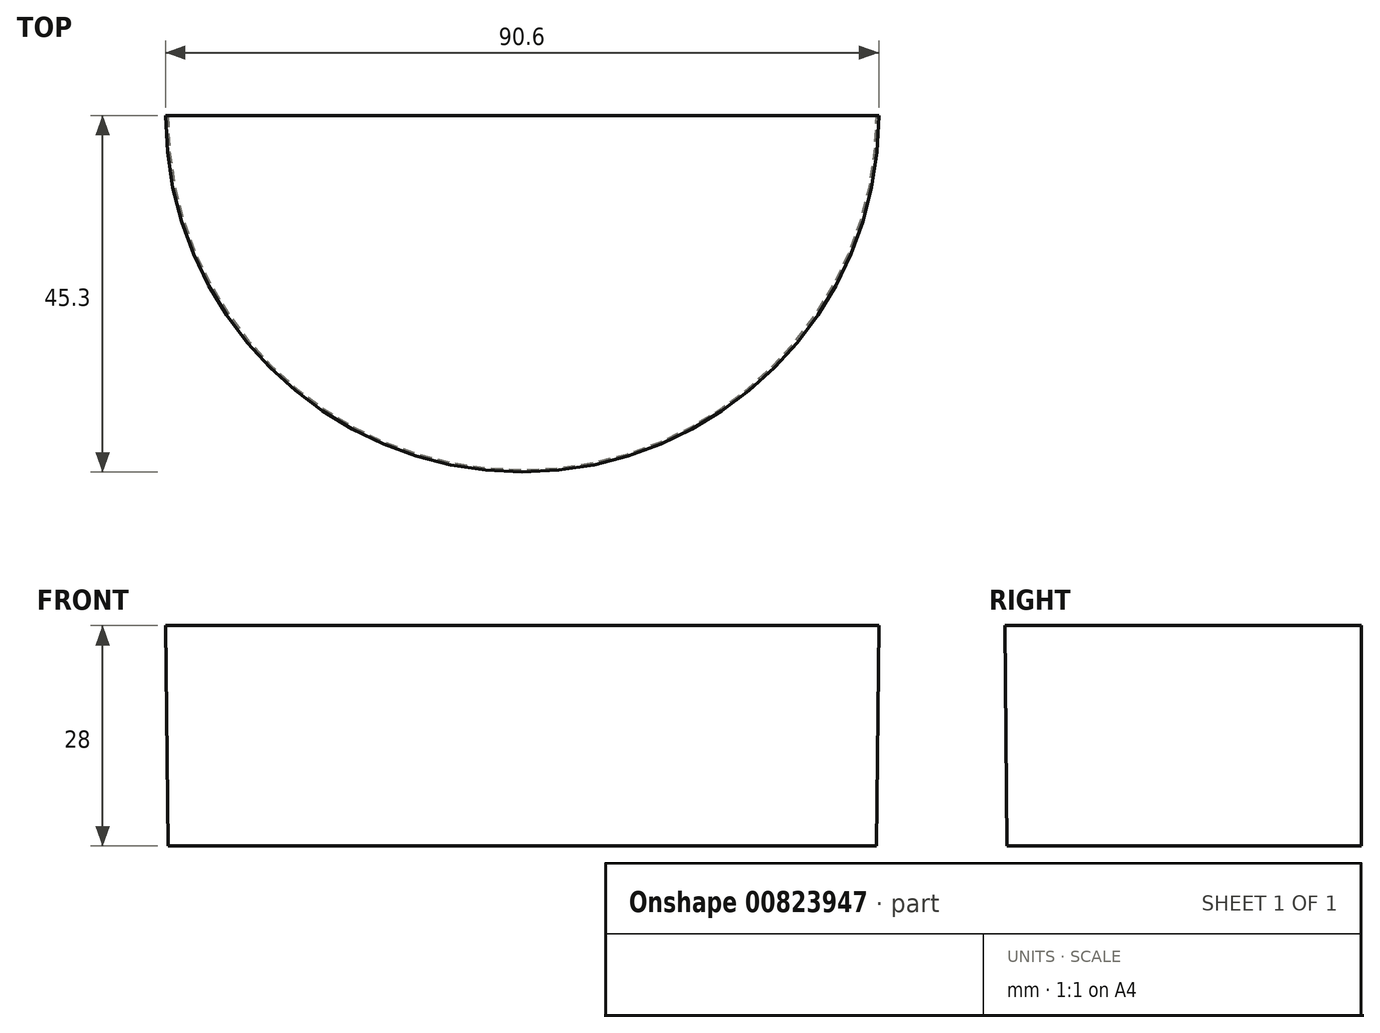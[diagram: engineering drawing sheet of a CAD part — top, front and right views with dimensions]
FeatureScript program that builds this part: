
annotation { "Feature Type Name" : "Feature", "Feature Type Description" : "" }
export const myFeature = defineFeature(function(context is Context, id is Id, definition is map)
    precondition{}
    {
        {
            var Q0;
            Q0=qCreatedBy(makeId("Front.planeOp"),FACE);
            var sketch = newSketch(context, id + "F0", { "sketchPlane" : qUnion([Q0])});
            skLineSegment(sketch, "E0", {"start": v(0, 0) * mm, "end": v(0, 19.11) * mm, "construction": true});
            skLineSegment(sketch, "E1", {"start": v(-45, 0) * mm, "end": v(-45.3, 28) * mm});
            skLineSegment(sketch, "E2", {"start": v(-45.3, 28) * mm, "end": v(0, 28) * mm});
            skLineSegment(sketch, "E3", {"start": v(0, 28) * mm, "end": v(0, 0) * mm});
            skLineSegment(sketch, "E4", {"start": v(-45, 0) * mm, "end": v(0, 0) * mm});
            skSolve(sketch);
        }
        {
            var Q0;
            Q0=makeQuery(id+"F0.imprint","IMPRINT",FACE,{"disambiguationData":[TD([[makeQuery(id+"F0.imprint","IMPRINT",EDGE,{"derivedFrom":sQuery(id+"F0.wireOp",EDGE,"E1")}),-1.0]])]});
            var Q1;
            Q1=sQuery(id+"F0.wireOp",EDGE,"E0");
            revolve(context, id + "F1", {"surfaceOperationType" : NewSurfaceOperationType.NEW, "entities" : qUnion([Q0]), "axis" : qUnion([Q1]), "revolveType" : RevolveType.ONE_DIRECTION, "angle" : 180 * degree});
        }
    });
